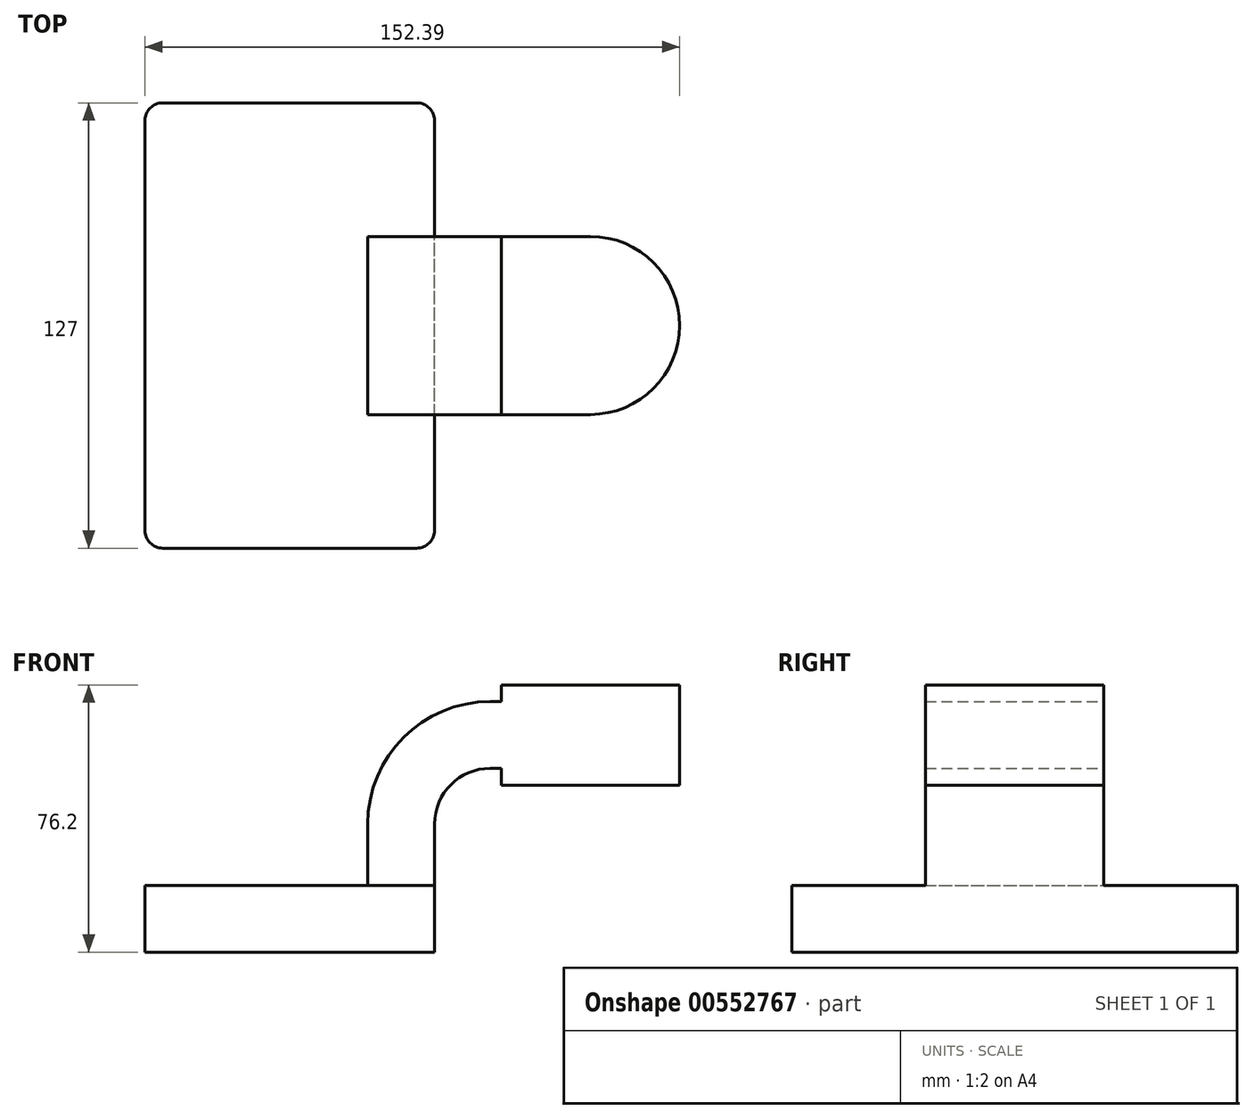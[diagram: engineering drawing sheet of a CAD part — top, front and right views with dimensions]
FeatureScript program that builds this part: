
annotation { "Feature Type Name" : "Feature", "Feature Type Description" : "" }
export const myFeature = defineFeature(function(context is Context, id is Id, definition is map)
    precondition{}
    {
        {
            var Q0;
            Q0=qCreatedBy(makeId("Front.planeOp"),FACE);
            var sketch = newSketch(context, id + "F0", { "sketchPlane" : qUnion([Q0])});
            skLineSegment(sketch, "E0.bottom", {"start": v(41.28, -9.52) * mm, "end": v(-41.28, -9.53) * mm});
            skLineSegment(sketch, "E0.top", {"start": v(41.28, 9.53) * mm, "end": v(-41.28, 9.53) * mm});
            skLineSegment(sketch, "E0.left", {"start": v(41.28, -9.52) * mm, "end": v(41.28, 9.53) * mm});
            skLineSegment(sketch, "E0.right", {"start": v(-41.28, -9.53) * mm, "end": v(-41.28, 9.53) * mm});
            skPoint(sketch, "E0.middle", {"position": v(0, 0) * mm});
            skLineSegment(sketch, "E1.bottom", {"start": v(111.12, 38.1) * mm, "end": v(60.32, 38.1) * mm});
            skLineSegment(sketch, "E1.top", {"start": v(111.12, 66.68) * mm, "end": v(60.32, 66.68) * mm});
            skLineSegment(sketch, "E1.left", {"start": v(111.12, 38.1) * mm, "end": v(111.12, 66.68) * mm});
            skLineSegment(sketch, "E1.right", {"start": v(60.32, 38.1) * mm, "end": v(60.32, 66.67) * mm});
            skPoint(sketch, "E1.middle", {"position": v(85.72, 52.39) * mm});
            skPoint(sketch, "E2.middle", {"position": v(81.68, 66.68) * mm});
            skLineSegment(sketch, "E3", {"start": v(41.28, 9.53) * mm, "end": v(41.28, 27) * mm});
            skArc(sketch, "E4", {"start": v(41.27, 27) * mm, "mid": v(45.92, 38.23) * mm, "end": v(57.15, 42.88) * mm});
            skLineSegment(sketch, "E5", {"start": v(57.15, 42.88) * mm, "end": v(85.16, 42.88) * mm});
            skLineSegment(sketch, "E6.0", {"start": v(57.15, 61.93) * mm, "end": v(85.16, 61.93) * mm});
            skArc(sketch, "E6.1", {"start": v(22.23, 27) * mm, "mid": v(32.45, 51.7) * mm, "end": v(57.15, 61.93) * mm});
            skLineSegment(sketch, "E6.2", {"start": v(22.22, 9.53) * mm, "end": v(22.22, 27) * mm});
            skLineSegment(sketch, "E7", {"start": v(85.72, 38.1) * mm, "end": v(85.72, 66.68) * mm});
            skFitSpline(sketch, "E8", {"points": [v(-41.28, 9.52) * mm, v(60.32, 66.67) * mm], "startDerivative": vector(19.48, 113.13) * mm, "endDerivative": vector(116.05, -35.17) * mm});
            skSolve(sketch);
        }
        {
            var Q0;
            Q0=makeQuery(id+"F0.imprint","IMPRINT",FACE,{"disambiguationData":[TD([[makeQuery(id+"F0.imprint","IMPRINT",EDGE,{"derivedFrom":sQuery(id+"F0.wireOp",EDGE,"E0.bottom")}),-1.0]])]});
            extrude(context, id + "F1", {"entities" : qUnion([Q0]), "endBound" : BoundingType.SYMMETRIC, "depth" : 127 * mm, "offsetDistance" : 25.4 * mm});
        }
        {
            var Q0;
            {var subQ1=sQuery(id+"F0.wireOp",EDGE,"E3");Q0=makeQuery(id+"F0.imprint","IMPRINT",FACE,{"disambiguationData":[TD([[makeQuery(id+"F0.imprint","IMPRINT",EDGE,{"derivedFrom":subQ1}),1.0]])]});}
            var Q1;
            {var subQ6=sQuery(id+"F0.wireOp",EDGE,"E7");Q1=makeQuery(id+"F0.imprint","IMPRINT",FACE,{"disambiguationData":[TD([[makeQuery(id+"F0.imprint","IMPRINT",EDGE,{"derivedFrom":subQ6}),1.0]])]});}
            extrude(context, id + "F2", {"entities" : qUnion([Q0, Q1]), "operationType" : NewBodyOperationType.ADD, "endBound" : BoundingType.SYMMETRIC, "depth" : 50.8 * mm, "offsetDistance" : 25.4 * mm});
        }
        {
            var Q0;
            {var subQ0=sQuery(id+"F0.wireOp",EDGE,"E6.1");Q0=makeQuery(id+"F0.imprint","IMPRINT",FACE,{"disambiguationData":[TD([[makeQuery(id+"F0.imprint","IMPRINT",EDGE,{"derivedFrom":subQ0}),1.0]])]});}
            extrude(context, id + "F3", {"entities" : qUnion([Q0]), "operationType" : NewBodyOperationType.ADD, "endBound" : BoundingType.SYMMETRIC, "depth" : 15.88 * mm, "offsetDistance" : 25.4 * mm});
        }
        {
            var Q0;
            {var subQ0=sQuery(id+"F0.wireOp",EDGE,"E1.left");Q0=makeQuery(id+"F0.imprint","IMPRINT",FACE,{"disambiguationData":[TD([[makeQuery(id+"F0.imprint","IMPRINT",EDGE,{"derivedFrom":subQ0}),1.0]])]});}
            var Q1;
            Q1=sQuery(id+"F0.wireOp",EDGE,"E7");
            revolve(context, id + "F4", {"operationType" : NewBodyOperationType.ADD, "entities" : qUnion([Q0]), "axis" : qUnion([Q1]), "revolveType" : RevolveType.FULL});
        }
        {
            var Q0;
            Q0=makeQuery(id+"F1.opExtrude","CAP_EDGE",EDGE,{"disambiguationData":[OSD([sQuery(id+"F0.wireOp",EDGE,"E0.left")])],"isStart":false});
            var Q1;
            Q1=makeQuery(id+"F1.opExtrude","CAP_EDGE",EDGE,{"disambiguationData":[OSD([sQuery(id+"F0.wireOp",EDGE,"E0.right")])],"isStart":false});
            var Q2;
            Q2=makeQuery(id+"F1.opExtrude","CAP_EDGE",EDGE,{"disambiguationData":[OSD([sQuery(id+"F0.wireOp",EDGE,"E0.right")])],"isStart":true});
            var Q3;
            Q3=makeQuery(id+"F1.opExtrude","CAP_EDGE",EDGE,{"disambiguationData":[OSD([sQuery(id+"F0.wireOp",EDGE,"E0.left")])],"isStart":true});
            fillet(context, id + "F5", {"entities" : qUnion([Q0, Q1, Q2, Q3]), "radius" : 5.08 * mm, "tangentPropagation" : true, "allowEdgeOverflow" : false});
        }
    });
